# Revit family: Montageschiene 35- 35-1,0 fbv 2m Langloch 2D
name_source: partatom
category: HLS-Bauteile
units: mm (PartAtom-declared; Revit-internal decimal feet)

## family parameters
Arbeitsebenenbasiert = Ja
Beim Laden mit Abzugskörper schneiden = Nein
Bemaßung runder Anschluss = Durchmesser verwenden
Beschriftungsausrichtung beibehalten = Nein
Gemeinsam genutzt = Ja
Immer vertikal = Nein
Raumberechnungspunkt = Nein
Teiletyp = Normal

## types (1)
- Stex 35- 35-1,0 fbv L=2000
    Abmessung = 35/35/1.0 mm
    Artikelnummer = 1273538
    Breite = 35 mm  [stored 0.114829 ft]
    Bund = 252 m
    EAN = 4250928424433
    Fabrikat = MEFA
    Firma = MEFA Befestigungs- und Montagesysteme GmbH
    Fläche (schwächster Profilquerschnitt) = 0 m²
    Gewicht = 1,03 kg
    Höhe = 35 mm
    Kurztext1 = Montageschiene C-Profil Stex
    Kurztext2 = 35 / 35 / 1 mm L= 2 m fbv
    Langloch = 8.5 x 15.0 mm
    Lochdurchmesser = 8.5 mm
    Lochdurchmesser 1 = 9 mm  [stored 0.0295276 ft]
    Lochdurchmesser 2 = 11 mm
    Länge = 2000 mm  [stored 6.56168 ft]
    Material = Stahl
    Materialname = S250
    Mengeneinheit = m
    Oberflaeche = feuerbandverzinkt
    Profil = C-Profil
    Profiltyp = 35/35
    Schlitzbreite = 21 mm
    Schwerpunktabstand eo = 1.72 cm
    Schwerpunktabstand eu = 1.78 cm
    Schwerpunktabstand ez = 1.75 cm
    Streckgrenze = 250 N/mm²
    Stärke = 1 mm  [stored 0.00328084 ft]
    Torsionswiderstandsmoment Wt = cm³
    Trägheitsradius iy = 1.34 cm
    Trägheitsradius iz = 1.46 cm
    Vorgabe-Ansicht = 1219 mm
    Widerstandsmoment Wy = 1.04 cm³
    Widerstandsmoment Wz = 1.26 cm³
    vpe = 12

note: [stored X ft] marks values corroborated as IEEE doubles in the binary element streams (Revit-internal decimal feet)
